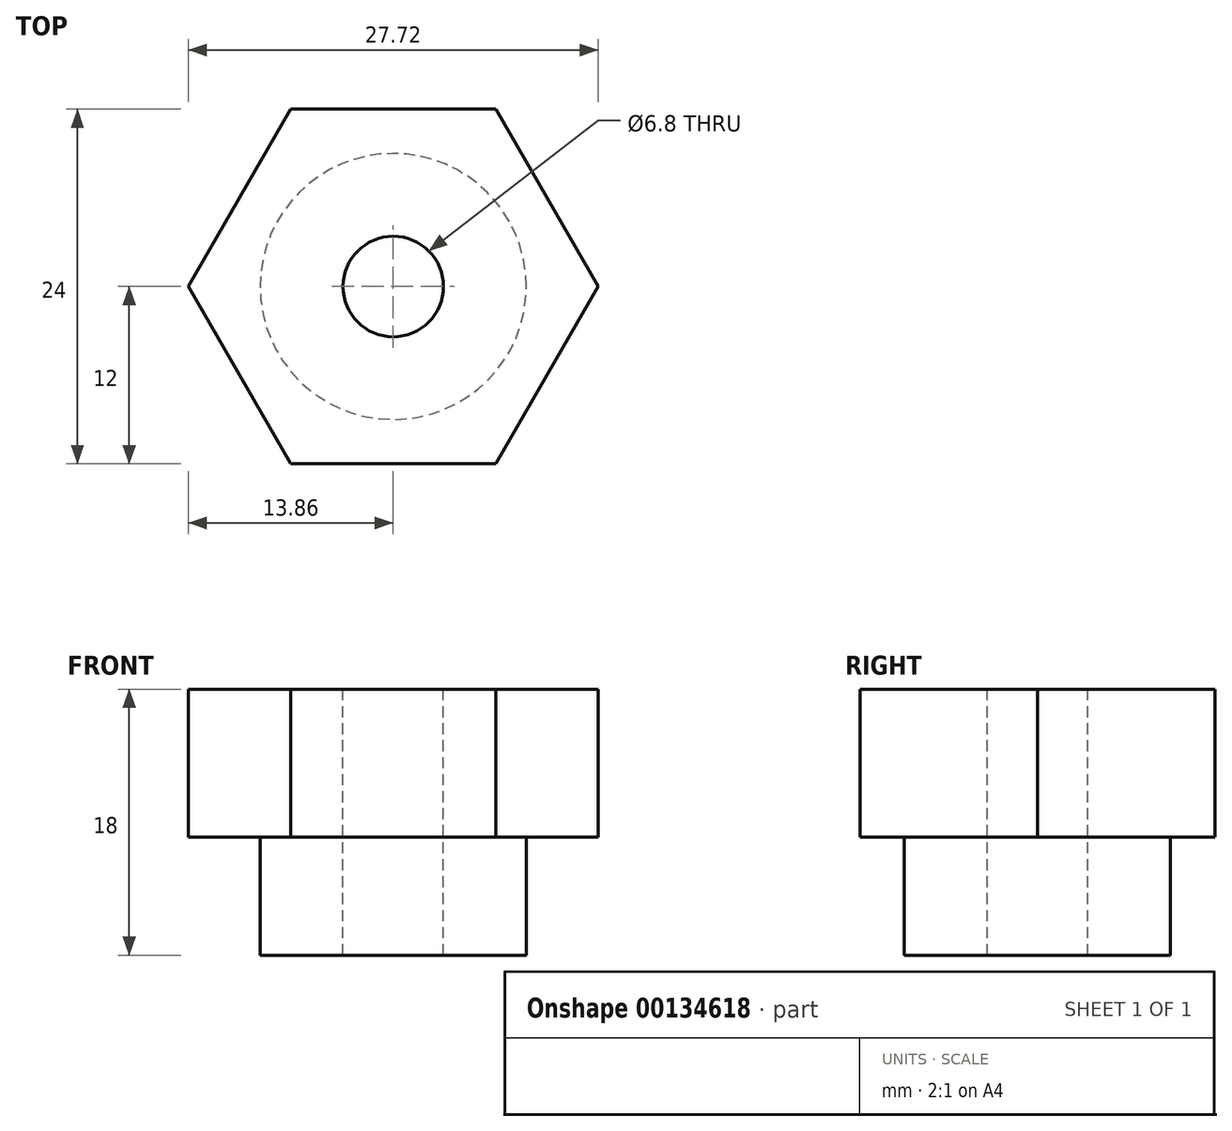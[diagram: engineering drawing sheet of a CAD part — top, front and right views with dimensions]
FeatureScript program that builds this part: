
annotation { "Feature Type Name" : "Feature", "Feature Type Description" : "" }
export const myFeature = defineFeature(function(context is Context, id is Id, definition is map)
    precondition{}
    {
        {
            var Q0;
            Q0=qCreatedBy(makeId("Top.planeOp"),FACE);
            var sketch = newSketch(context, id + "F0", { "sketchPlane" : qUnion([Q0])});
            skCircle(sketch, "E0.cCircle", {"center": v(0, 0) * mm, "radius": 12 * mm, "construction": true});
            skLineSegment(sketch, "E0.0", {"start": v(-6.93, 12) * mm, "end": v(6.93, 12) * mm});
            skLineSegment(sketch, "E0.1", {"start": v(6.93, 12) * mm, "end": v(13.86, 0) * mm});
            skLineSegment(sketch, "E0.2", {"start": v(13.86, 0) * mm, "end": v(6.93, -12) * mm});
            skLineSegment(sketch, "E0.3", {"start": v(6.93, -12) * mm, "end": v(-6.93, -12) * mm});
            skLineSegment(sketch, "E0.4", {"start": v(-6.93, -12) * mm, "end": v(-13.86, 0) * mm});
            skLineSegment(sketch, "E0.5", {"start": v(-13.86, 0) * mm, "end": v(-6.93, 12) * mm});
            skPoint(sketch, "E0.0.midPoint", {"position": v(0, 12) * mm});
            skSolve(sketch);
        }
        {
            var Q0;
            Q0=makeQuery(id+"F0.imprint","IMPRINT",FACE,{"disambiguationData":[TD([[makeQuery(id+"F0.imprint","IMPRINT",EDGE,{"derivedFrom":sQuery(id+"F0.wireOp",EDGE,"E0.0")}),-1.0]])]});
            extrude(context, id + "F1", {"entities" : qUnion([Q0]), "depth" : 10 * mm});
        }
        {
            var Q0;
            Q0=makeQuery(id+"F1.opExtrude","CAP_FACE",FACE,{"disambiguationData":[OSD([sQuery(id+"F0.wireOp",EDGE,"E0.0"),sQuery(id+"F0.wireOp",EDGE,"E0.1"),sQuery(id+"F0.wireOp",EDGE,"E0.2"),sQuery(id+"F0.wireOp",EDGE,"E0.3"),sQuery(id+"F0.wireOp",EDGE,"E0.4"),sQuery(id+"F0.wireOp",EDGE,"E0.5")])],"isStart":true});
            var sketch = newSketch(context, id + "F2", { "sketchPlane" : qUnion([Q0])});
            skCircle(sketch, "E1", {"center": v(0, 0) * mm, "radius": 9 * mm});
            skSolve(sketch);
        }
        {
            var Q0;
            Q0=makeQuery(id+"F2.imprint","IMPRINT",FACE,{"disambiguationData":[TD([[makeQuery(id+"F2.imprint","IMPRINT",EDGE,{"derivedFrom":sQuery(id+"F2.wireOp",EDGE,"E1")}),1.0]])]});
            extrude(context, id + "F3", {"entities" : qUnion([Q0]), "operationType" : NewBodyOperationType.ADD, "depth" : 8 * mm});
        }
        {
            var Q0;
            Q0=makeQuery(id+"F1.opExtrude","CAP_FACE",FACE,{"disambiguationData":[OSD([sQuery(id+"F0.wireOp",EDGE,"E0.0"),sQuery(id+"F0.wireOp",EDGE,"E0.1"),sQuery(id+"F0.wireOp",EDGE,"E0.2"),sQuery(id+"F0.wireOp",EDGE,"E0.3"),sQuery(id+"F0.wireOp",EDGE,"E0.4"),sQuery(id+"F0.wireOp",EDGE,"E0.5")])],"isStart":false});
            var sketch = newSketch(context, id + "F4", { "sketchPlane" : qUnion([Q0])});
            skCircle(sketch, "E2", {"center": v(0, 0) * mm, "radius": 3.4 * mm});
            skSolve(sketch);
        }
        {
            var Q0;
            Q0=makeQuery(id+"F4.imprint","IMPRINT",FACE,{"disambiguationData":[TD([[makeQuery(id+"F4.imprint","IMPRINT",EDGE,{"derivedFrom":sQuery(id+"F4.wireOp",EDGE,"E2")}),1.0]])]});
            extrude(context, id + "F5", {"entities" : qUnion([Q0]), "operationType" : NewBodyOperationType.REMOVE, "oppositeDirection" : true, "depth" : 25 * mm});
        }
    });
